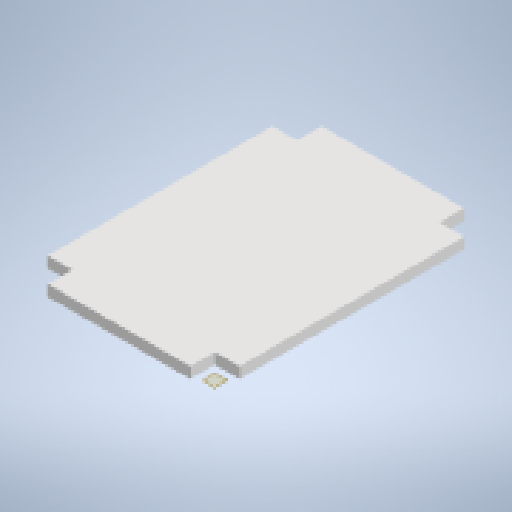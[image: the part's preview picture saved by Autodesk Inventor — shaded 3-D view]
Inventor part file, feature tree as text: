
AUTODESK INVENTOR PART (.ipt)
format: ipt  version: 2024 (Build 280153000, 153)  size: 144,384 bytes
history: native  units: mm
features: sketch x1, plane x1, extrude x1
ambient origin geometry x8: Origin, YZ Plane, XZ Plane, XY Plane, X Axis, Y Axis, Z Axis, Center Point
bodies: Body1 (feature_tree)
feature tree (3):
  sketch  "Sketch2"  dims[d0=350.0mm d1=500.0mm d12=45.0mm d13=45.0mm d14=45.0mm d15=45.0mm d16=45.0mm d17=45.0mm d18=45.0mm d19=45.0mm d20=20.0mm d21=0.0mm]
  plane  "Work Plane1"
  extrude  "Extrusion2"  Depth=500.0mm
